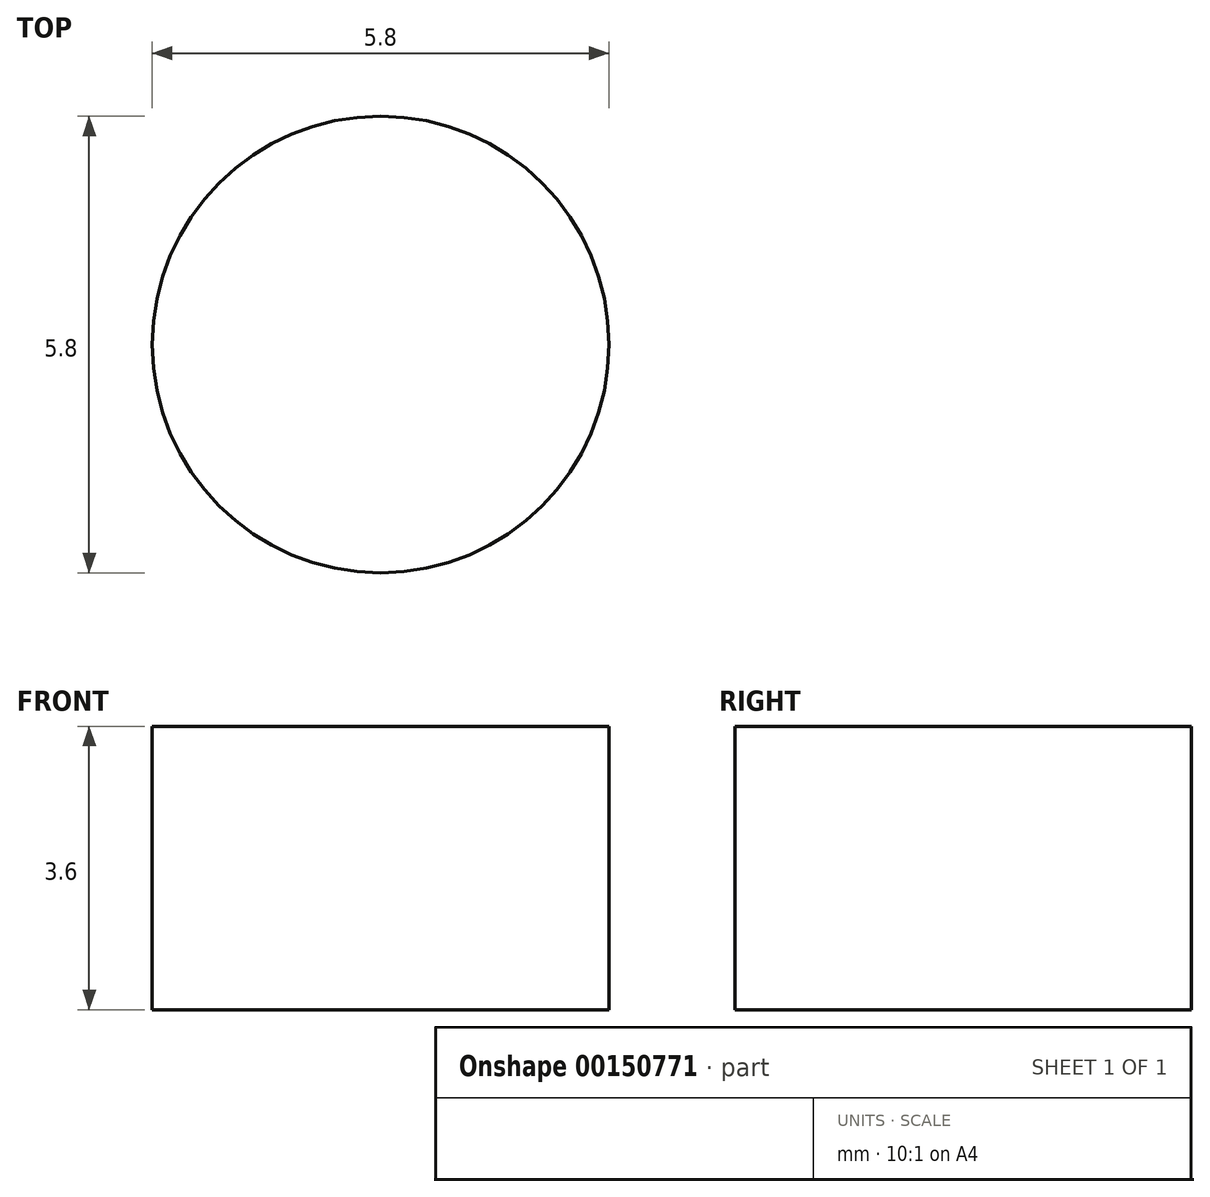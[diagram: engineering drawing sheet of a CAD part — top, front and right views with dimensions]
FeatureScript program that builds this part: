
annotation { "Feature Type Name" : "Feature", "Feature Type Description" : "" }
export const myFeature = defineFeature(function(context is Context, id is Id, definition is map)
    precondition{}
    {
        {
            var Q0;
            Q0=qCreatedBy(makeId("Top.planeOp"),FACE);
            var sketch = newSketch(context, id + "F0", { "sketchPlane" : qUnion([Q0])});
            skCircle(sketch, "E0", {"center": v(0, 0) * mm, "radius": 2.9 * mm});
            skSolve(sketch);
        }
        {
            var Q0;
            Q0 = qSketchRegion(id + "F0", true);
            extrude(context, id + "F1", {"entities" : qUnion([Q0]), "depth" : 3.6 * mm});
        }
    });
